# Revit family: Lighting-Terziario-GEWISS-ELIA-PL-LED_INCASSO
name_source: partatom
category: Apparecchi per illuminazione
units: mm (PartAtom-declared; Revit-internal decimal feet)

## family parameters
Condiviso = No
Host = Superficie
Punto di calcolo locali = Sì
Quota connettore circolare = Usa diametro
Sorgente d'illuminazione = Sì
Taglio con vuoti quando caricato = No
Tipo di parte = Normale

## types (48) — shared parameters
Angolo inclinazione = -90.00°
Applicazione = Interno
BORDO = BORDO
Catalogo = LIGHTING
Catalogo Serie = ELIA PL
Classe isolamento = II
Colore = Bianco
Emetti da lunghezza linea = 610 mm
FORO_CONTROSOFFITTO = 80 mm  [stored 0.262467 ft]
File diagramma fotometrico = GWF1611NN940.IES
Filtro dei colori = 16777215
Garanzia = 5 anni
Grado di protezione = IP20 - IP40
IDF = 6d914e3b-5f92-4411-bf6e-4fbd694a4409
IDT = 4c6a4f10-3f0b-4303-adcc-d543444cbb8d
Immagine tipo = ELIA_PL_q.jpg
Installazione = Incasso modulare
LED Life time (L80B50) = L80 B50 (Tq25°) = 50.000h
L_lampada = 1500 mm  [stored 4.92126 ft]
Lampada: = LED
Larghezza lampada = 620 mm  [stored 2.03412 ft]
Lunghezza lampada = 620 mm  [stored 2.03412 ft]
POSIZIONE = 80000
Potenza di sistema = 33W
Produttore = GEWISS S.p.A.
Prospetto di default = 1219 mm
Resistenza agli urti = IK03
SCHERMO LED = SCHERMO LED
SEO = Incasso modulare
Scheda Tecnica = https://www.gewiss.com
Temperatura di funzionamento = -20° +45°
Temperatura di utilizzo = -20° +45°
Tensione = 220-240 VÂ
Tipo lampada = LED
Tipologia = Incasso modulare
Tipologia sorgente luminosa = LED - Non sostituibile
URL = https://www.gewiss.com
Variazione temperatura colore lampada con luminosità attenuata = <Nessuno>
Versione file RFA = 20.0
corpo centrale = corpo centrale

## per-type parameters (varying)
| type | Descrizione | Dimensioni (mm) | Lumen output (lm) | Modello | Ottica | Peso (kg) | Peso (kg): | Temperatura di colore | Temperatura di colore: | UGR: |
| GWF1611LA930 - ELIA PL M1 OPAL 30K DALI CRI90 | ELIA PL M1 OPAL 30K DALI CRI90 | 30x120 | 3500 | GWF1611LA930 | Opale diffondente | 2,4 | 2,4 | 3000K | 3000K | UGR<22 |
| GWF1610LA940 - ELIA PL M1 OPAL 40K ON/OFF CRI90 | ELIA PL M1 OPAL 40K ON/OFF CRI90 | 30x120 | 3700 | GWF1610LA940 | Opale diffondente | 2,4 | 2,4 | 4000K | 4000K | UGR<22 |
| GWF1610NN940 - ELIA PL M3 MICROP.40K ON/OFF CRI90 | ELIA PL M3 MICROP.40K ON/OFF CRI90 | 62x62 | 3300 | GWF1610NN940 | Microprismato | 2,6 | 2,6 | 4000K | 4000K | UGR<19 |
| GWF1610NA930 - ELIA PL M3 OPAL 30K ON/OFF CRI90 | ELIA PL M3 OPAL 30K ON/OFF CRI90 | 62x62 | 3500 | GWF1610NA930 | Opale diffondente | 2,6 | 2,6 | 3000K | 3000K | UGR<22 |
| GWF1611NN840 - ELIA PL M3 MICROP.40K DALI CRI80 | ELIA PL M3 MICROP.40K DALI CRI80 | 62x62 | 3600 | GWF1611NN840 | Microprismato | 2,6 | 2,6 | 4000K | 4000K | UGR<19 |
| GWF1610NA830 - ELIA PL M3 OPAL 30K ON/OFF CRI80 | ELIA PL M3 OPAL 30K ON/OFF CRI80 | 62x62 | 3700 | GWF1610NA830 | Opale diffondente | 2,6 | 2,6 | 3000K | 3000K | UGR<22 |
| GWF1610MA840 - ELIA PL M2 OPAL 40K ON/OFF CRI80 | ELIA PL M2 OPAL 40K ON/OFF CRI80 | 60x60 | 3900 | GWF1610MA840 | Opale diffondente | 2,4 | 2,4 | 4000K | 4000K | UGR<22 |
| GWF1610MN840 - ELIA PL M2 MICROP.40K ON/OFF CRI80 | ELIA PL M2 MICROP.40K ON/OFF CRI80 | 60x60 | 3600 | GWF1610MN840 | Microprismato | 2,4 | 2,4 | 4000K | 4000K | UGR<19 |
| GWF1610NN830 - ELIA PL M3 MICROP.30K ON/OFF CRI80 | ELIA PL M3 MICROP.30K ON/OFF CRI80 | 62x62 | 3300 | GWF1610NN830 | Microprismato | 2,6 | 2,6 | 3000K | 3000K | UGR<19 |
| GWF1610MA940 - ELIA PL M2 OPAL 40K ON/OFF CRI90 | ELIA PL M2 OPAL 40K ON/OFF CRI90 | 60x60 | 3700 | GWF1610MA940 | Opale diffondente | 2,4 | 2,4 | 4000K | 4000K | UGR<22 |
| GWF1610MA830 - ELIA PL M2 OPAL 30K ON/OFF CRI80 | ELIA PL M2 OPAL 30K ON/OFF CRI80 | 60x60 | 3700 | GWF1610MA830 | Opale diffondente | 2,4 | 2,4 | 3000K | 3000K | UGR<22 |
| GWF1611LA940 - ELIA PL M1 OPAL 40K DALI CRI90 | ELIA PL M1 OPAL 40K DALI CRI90 | 30x120 | 3700 | GWF1611LA940 | Opale diffondente | 2,4 | 2,4 | 4000K | 4000K | UGR<22 |
| GWF1610LN840 - ELIA PL M1 MICROP.40K ON/OFF CRI80 | ELIA PL M1 MICROP.40K ON/OFF CRI80 | 30x120 | 3600 | GWF1610LN840 | Microprismato | 2,4 | 2,4 | 4000K | 4000K | UGR<19 |
| GWF1611LN830 - ELIA PL M1 MICROP.30K DALI CRI80 | ELIA PL M1 MICROP.30K DALI CRI80 | 30x120 | 3300 | GWF1611LN830 | Microprismato | 2,4 | 2,4 | 3000K | 3000K | UGR<19 |
| GWF1610MN940 - ELIA PL M2 MICROP.40K ON/OFF CRI90 | ELIA PL M2 MICROP.40K ON/OFF CRI90 | 60x60 | 3300 | GWF1610MN940 | Microprismato | 2,4 | 2,4 | 4000K | 4000K | UGR<19 |
| GWF1610NA840 - ELIA PL M3 OPAL 40K ON/OFF CRI80 | ELIA PL M3 OPAL 40K ON/OFF CRI80 | 62x62 | 3900 | GWF1610NA840 | Opale diffondente | 2,6 | 2,6 | 4000K | 4000K | UGR<22 |
| GWF1610NN930 - ELIA PL M3 MICROP.30K ON/OFF CRI90 | ELIA PL M3 MICROP.30K ON/OFF CRI90 | 62x62 | 3000 | GWF1610NN930 | Microprismato | 2,6 | 2,6 | 3000K | 3000K | UGR<19 |
| GWF1611MA930 - ELIA PL M2 OPAL 30K DALI CRI90 | ELIA PL M2 OPAL 30K DALI CRI90 | 60x60 | 3500 | GWF1611MA930 | Opale diffondente | 2,4 | 2,4 | 3000K | 3000K | UGR<22 |
| GWF1611NA940 - ELIA PL M3 OPAL 40K DALI CRI90 | ELIA PL M3 OPAL 40K DALI CRI90 | 62x62 | 3700 | GWF1611NA940 | Opale diffondente | 2,6 | 2,6 | 4000K | 4000K | UGR<22 |
| GWF1610MN830 - ELIA PL M2 MICROP.30K ON/OFF CRI80 | ELIA PL M2 MICROP.30K ON/OFF CRI80 | 60x60 | 3300 | GWF1610MN830 | Microprismato | 2,4 | 2,4 | 3000K | 3000K | UGR<19 |
| GWF1611LN840 - ELIA PL M1 MICROP.40K DALI CRI80 | ELIA PL M1 MICROP.40K DALI CRI80 | 30x120 | 3600 | GWF1611LN840 | Microprismato | 2,4 | 2,4 | 4000K | 4000K | UGR<19 |
| GWF1610MN930 - ELIA PL M2 MICROP.30K ON/OFF CRI90 | ELIA PL M2 MICROP.30K ON/OFF CRI90 | 60x60 | 3000 | GWF1610MN930 | Microprismato | 2,4 | 2,4 | 3000K | 3000K | UGR<19 |
| GWF1610LA830 - ELIA PL M1 OPAL 30K ON/OFF CRI80 | ELIA PL M1 OPAL 30K ON/OFF CRI80 | 30x120 | 3700 | GWF1610LA830 | Opale diffondente | 2,4 | 2,4 | 3000K | 3000K | UGR<22 |
| GWF1611NN830 - ELIA PL M3 MICROP.30K DALI CRI80 | ELIA PL M3 MICROP.30K DALI CRI80 | 62x62 | 3300 | GWF1611NN830 | Microprismato | 2,6 | 2,6 | 3000K | 3000K | UGR<19 |
| GWF1611MN830 - ELIA PL M2 MICROP.30K DALI CRI80 | ELIA PL M2 MICROP.30K DALI CRI80 | 60x60 | 3300 | GWF1611MN830 | Microprismato | 2,4 | 2,4 | 3000K | 3000K | UGR<19 |
| GWF1611NA930 - ELIA PL M3 OPAL 30K DALI CRI90 | ELIA PL M3 OPAL 30K DALI CRI90 | 62x62 | 3500 | GWF1611NA930 | Opale diffondente | 2,6 | 2,6 | 3000K | 3000K | UGR<22 |
| GWF1611MA940 - ELIA PL M2 OPAL 40K DALI CRI90 | ELIA PL M2 OPAL 40K DALI CRI90 | 60x60 | 3700 | GWF1611MA940 | Opale diffondente | 2,4 | 2,4 | 4000K | 4000K | UGR<22 |
| GWF1610LN930 - ELIA PL M1 MICROP.30K ON/OFF CRI90 | ELIA PL M1 MICROP.30K ON/OFF CRI90 | 30x120 | 3000 | GWF1610LN930 | Microprismato | 2,4 | 2,4 | 3000K | 3000K | UGR<19 |
| GWF1611NA830 - ELIA PL M3 OPAL 30K DALI CRI80 | ELIA PL M3 OPAL 30K DALI CRI80 | 62x62 | 3700 | GWF1611NA830 | Opale diffondente | 2,6 | 2,6 | 3000K | 3000K | UGR<22 |
| GWF1610MA930 - ELIA PL M2 OPAL 30K ON/OFF CRI90 | ELIA PL M2 OPAL 30K ON/OFF CRI90 | 60x60 | 3500 | GWF1610MA930 | Opale diffondente | 2,4 | 2,4 | 3000K | 3000K | UGR<22 |
| GWF1611LA830 - ELIA PL M1 OPAL 30K DALI CRI80 | ELIA PL M1 OPAL 30K DALI CRI80 | 30x120 | 3700 | GWF1611LA830 | Opale diffondente | 2,4 | 2,4 | 3000K | 3000K | UGR<22 |
| GWF1610LA840 - ELIA PL M1 OPAL 40K ON/OFF CRI80 | ELIA PL M1 OPAL 40K ON/OFF CRI80 | 30x120 | 3900 | GWF1610LA840 | Opale diffondente | 2,4 | 2,4 | 4000K | 4000K | UGR<22 |
| GWF1611LN940 - ELIA PL M1 MICROP.40K DALI CRI90 | ELIA PL M1 MICROP.40K DALI CRI90 | 30x120 | 3300 | GWF1611LN940 | Microprismato | 2,4 | 2,4 | 4000K | 4000K | UGR<19 |
| GWF1611MA830 - ELIA PL M2 OPAL 30K DALI CRI80 | ELIA PL M2 OPAL 30K DALI CRI80 | 60x60 | 3700 | GWF1611MA830 | Opale diffondente | 2,4 | 2,4 | 3000K | 3000K | UGR<22 |
| GWF1611NA840 - ELIA PL M3 OPAL 40K DALI CRI80 | ELIA PL M3 OPAL 40K DALI CRI80 | 62x62 | 3900 | GWF1611NA840 | Opale diffondente | 2,6 | 2,6 | 4000K | 4000K | UGR<22 |
| GWF1611MA840 - ELIA PL M2 OPAL 40K DALI CRI80 | ELIA PL M2 OPAL 40K DALI CRI80 | 60x60 | 3900 | GWF1611MA840 | Opale diffondente | 2,4 | 2,4 | 4000K | 4000K | UGR<22 |
| GWF1611NN940 - ELIA PL M3 MICROP.40K DALI CRI90 | ELIA PL M3 MICROP.40K DALI CRI90 | 62x62 | 3300 | GWF1611NN940 | Microprismato | 2,6 | 2,6 | 4000K | 4000K | UGR<19 |
| GWF1610NN840 - ELIA PL M3 MICROP.40K ON/OFF CRI80 | ELIA PL M3 MICROP.40K ON/OFF CRI80 | 62x62 | 3600 | GWF1610NN840 | Microprismato | 2,6 | 2,6 | 4000K | 4000K | UGR<19 |
| GWF1611MN840 - ELIA PL M2 MICROP.40K DALI CRI80 | ELIA PL M2 MICROP.40K DALI CRI80 | 60x60 | 3600 | GWF1611MN840 | Microprismato | 2,4 | 2,4 | 4000K | 4000K | UGR<19 |
| GWF1610LA930 - ELIA PL M1 OPAL 30K ON/OFF CRI90 | ELIA PL M1 OPAL 30K ON/OFF CRI90 | 30x120 | 3500 | GWF1610LA930 | Opale diffondente | 2,4 | 2,4 | 3000K | 3000K | UGR<22 |
| GWF1611MN940 - ELIA PL M2 MICROP.40K DALI CRI90 | ELIA PL M2 MICROP.40K DALI CRI90 | 60x60 | 3300 | GWF1611MN940 | Microprismato | 2,4 | 2,4 | 4000K | 4000K | UGR<19 |
| GWF1611LN930 - ELIA PL M1 MICROP.30K DALI CRI90 | ELIA PL M1 MICROP.30K DALI CRI90 | 30x120 | 3000 | GWF1611LN930 | Microprismato | 2,4 | 2,4 | 3000K | 3000K | UGR<19 |
| GWF1610NA940 - ELIA PL M3 OPAL 40K ON/OFF CRI90 | ELIA PL M3 OPAL 40K ON/OFF CRI90 | 62x62 | 3700 | GWF1610NA940 | Opale diffondente | 2,6 | 2,6 | 4000K | 4000K | UGR<22 |
| GWF1610LN940 - ELIA PL M1 MICROP.40K ON/OFF CRI90 | ELIA PL M1 MICROP.40K ON/OFF CRI90 | 30x120 | 3300 | GWF1610LN940 | Microprismato | 2,4 | 2,4 | 4000K | 4000K | UGR<19 |
| GWF1611NN930 - ELIA PL M3 MICROP.30K DALI CRI90 | ELIA PL M3 MICROP.30K DALI CRI90 | 62x62 | 3000 | GWF1611NN930 | Microprismato | 2,6 | 2,6 | 3000K | 3000K | UGR<19 |
| GWF1611LA840 - ELIA PL M1 OPAL 40K DALI CRI80 | ELIA PL M1 OPAL 40K DALI CRI80 | 30x120 | 3900 | GWF1611LA840 | Opale diffondente | 2,4 | 2,4 | 4000K | 4000K | UGR<22 |
| GWF1611MN930 - ELIA PL M2 MICROP.30K DALI CRI90 | ELIA PL M2 MICROP.30K DALI CRI90 | 60x60 | 3000 | GWF1611MN930 | Microprismato | 2,4 | 2,4 | 3000K | 3000K | UGR<19 |
| GWF1610LN830 - ELIA PL M1 MICROP.30K ON/OFF CRI80 | ELIA PL M1 MICROP.30K ON/OFF CRI80 | 30x120 | 3300 | GWF1610LN830 | Microprismato | 2,4 | 2,4 | 3000K | 3000K | UGR<19 |

note: [stored X ft] marks values corroborated as IEEE doubles in the binary element streams (Revit-internal decimal feet)
